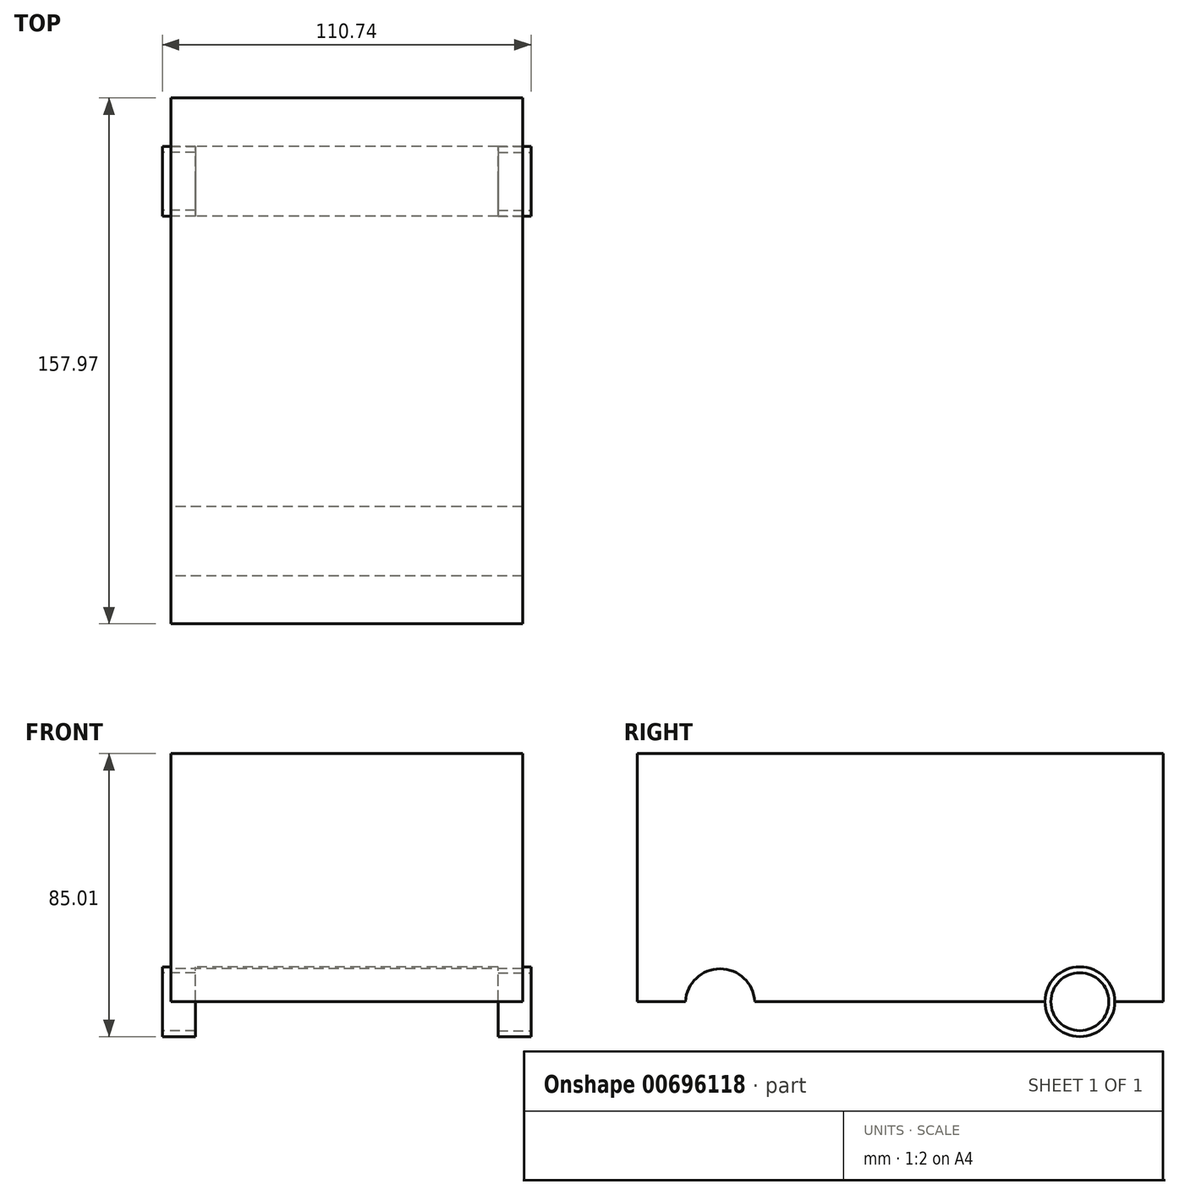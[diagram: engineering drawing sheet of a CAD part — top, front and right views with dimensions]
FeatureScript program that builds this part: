
annotation { "Feature Type Name" : "Feature", "Feature Type Description" : "" }
export const myFeature = defineFeature(function(context is Context, id is Id, definition is map)
    precondition{}
    {
        {
            var Q0;
            Q0=qCreatedBy(makeId("Right.planeOp"),FACE);
            var sketch = newSketch(context, id + "F0", { "sketchPlane" : qUnion([Q0])});
            skLineSegment(sketch, "E0.bottom", {"start": v(78.11, 62.93) * mm, "end": v(-79.86, 62.93) * mm});
            skLineSegment(sketch, "E0.top", {"start": v(78.11, -11.53) * mm, "end": v(-79.86, -11.53) * mm});
            skLineSegment(sketch, "E0.left", {"start": v(78.11, 62.93) * mm, "end": v(78.11, -11.53) * mm});
            skLineSegment(sketch, "E0.right", {"start": v(-79.86, 62.93) * mm, "end": v(-79.86, -11.53) * mm});
            skSolve(sketch);
        }
        {
            var Q0;
            Q0=makeQuery(id+"F0.imprint","IMPRINT",FACE,{"disambiguationData":[TD([[makeQuery(id+"F0.imprint","IMPRINT",EDGE,{"derivedFrom":sQuery(id+"F0.wireOp",EDGE,"E0.bottom")}),1.0]])]});
            extrude(context, id + "F1", {"entities" : qUnion([Q0]), "depth" : 52.83 * mm, "offsetDistance" : 25.4 * mm});
        }
        {
            var Q0;
            Q0=qCreatedBy(makeId("Right.planeOp"),FACE);
            var sketch = newSketch(context, id + "F2", { "sketchPlane" : qUnion([Q0])});
            skCircle(sketch, "E1", {"center": v(-55.04, -12.12) * mm, "radius": 7.64 * mm});
            skCircle(sketch, "E2", {"center": v(-55.04, -12.12) * mm, "radius": 10.42 * mm});
            skCircle(sketch, "E3", {"center": v(53.01, -11.6) * mm, "radius": 10.48 * mm});
            skCircle(sketch, "E4", {"center": v(53.01, -11.6) * mm, "radius": 8.7 * mm});
            skPoint(sketch, "E5.center.orphan", {"position": v(-42.72, 0) * mm});
            skPoint(sketch, "E6.center.orphan", {"position": v(-42.72, -6.92) * mm});
            skSolve(sketch);
        }
        {
            var Q0;
            Q0=makeQuery(id+"F2.imprint","IMPRINT",FACE,{"disambiguationData":[TD([[makeQuery(id+"F2.imprint","IMPRINT",EDGE,{"derivedFrom":sQuery(id+"F2.wireOp",EDGE,"E4")}),1.0]])]});
            var Q1;
            Q1=makeQuery(id+"F2.imprint","IMPRINT",FACE,{"disambiguationData":[TD([[makeQuery(id+"F2.imprint","IMPRINT",EDGE,{"derivedFrom":sQuery(id+"F2.wireOp",EDGE,"E3")}),1.0]])]});
            var Q2;
            Q2=makeQuery(id+"F2.imprint","IMPRINT",FACE,{"disambiguationData":[TD([[makeQuery(id+"F2.imprint","IMPRINT",EDGE,{"derivedFrom":sQuery(id+"F2.wireOp",EDGE,"E1")}),1.0]])]});
            var Q3;
            Q3=makeQuery(id+"F2.imprint","IMPRINT",FACE,{"disambiguationData":[TD([[makeQuery(id+"F2.imprint","IMPRINT",EDGE,{"derivedFrom":sQuery(id+"F2.wireOp",EDGE,"E1")}),-1.0]])]});
            extrude(context, id + "F3", {"entities" : qUnion([Q0, Q1, Q2, Q3]), "operationType" : NewBodyOperationType.REMOVE, "depth" : 66.8 * mm, "offsetDistance" : 25.4 * mm});
        }
        {
            var Q0;
            Q0=makeQuery(id+"F2.imprint","IMPRINT",FACE,{"disambiguationData":[TD([[makeQuery(id+"F2.imprint","IMPRINT",EDGE,{"derivedFrom":sQuery(id+"F2.wireOp",EDGE,"E3")}),1.0]])]});
            extrude(context, id + "F4", {"entities" : qUnion([Q0]), "oppositeDirection" : true, "depth" : 9.9 * mm, "offsetDistance" : 25.4 * mm});
        }
        {
            var Q0;
            Q0=makeQuery(id+"F4.opExtrude","SWEPT_BODY",BODY,{"disambiguationData":[OSD([sQuery(id+"F2.wireOp",EDGE,"E3"),sQuery(id+"F2.wireOp",EDGE,"E4")])]});
            transform(context, id + "F5", {"entities" : qUnion([Q0]), "transformType" : TransformType.TRANSLATION_3D, "dx" : 55.37 * mm, "dy" : 0 * mm, "dz" : 0 * mm, "makeCopy" : false});
        }
        {
            var Q0;
            Q0=makeQuery(id+"F1.opExtrude","SWEPT_BODY",BODY,{"disambiguationData":[OSD([sQuery(id+"F0.wireOp",EDGE,"E0.bottom"),sQuery(id+"F0.wireOp",EDGE,"E0.top"),sQuery(id+"F0.wireOp",EDGE,"E0.left"),sQuery(id+"F0.wireOp",EDGE,"E0.right")])]});
            var Q1;
            Q1=makeQuery(id+"F1.opExtrude","CAP_FACE",FACE,{"disambiguationData":[OSD([sQuery(id+"F0.wireOp",EDGE,"E0.bottom"),sQuery(id+"F0.wireOp",EDGE,"E0.top"),sQuery(id+"F0.wireOp",EDGE,"E0.left"),sQuery(id+"F0.wireOp",EDGE,"E0.right")])],"isStart":true});
            mirror(context, id + "F6", {"operationType" : NewBodyOperationType.ADD, "entities" : qUnion([Q0]), "mirrorPlane" : qUnion([Q1])});
        }
        {
            var Q0;
            Q0=makeQuery(id+"F4.opExtrude","SWEPT_BODY",BODY,{"disambiguationData":[OSD([sQuery(id+"F2.wireOp",EDGE,"E3"),sQuery(id+"F2.wireOp",EDGE,"E4")])]});
            var Q1;
            Q1=qCreatedBy(makeId("Right.planeOp"),FACE);
            mirror(context, id + "F7", {"operationType" : NewBodyOperationType.ADD, "entities" : qUnion([Q0]), "mirrorPlane" : qUnion([Q1])});
        }
        {
            var Q0;
            Q0=sQuery(id+"F2.wireOp",EDGE,"E1");
            extrude(context, id + "F8", {"bodyType" : ToolBodyType.SURFACE, "surfaceEntities" : qUnion([Q0]), "depth" : 51.82 * mm, "offsetDistance" : 25.4 * mm});
        }
    });
